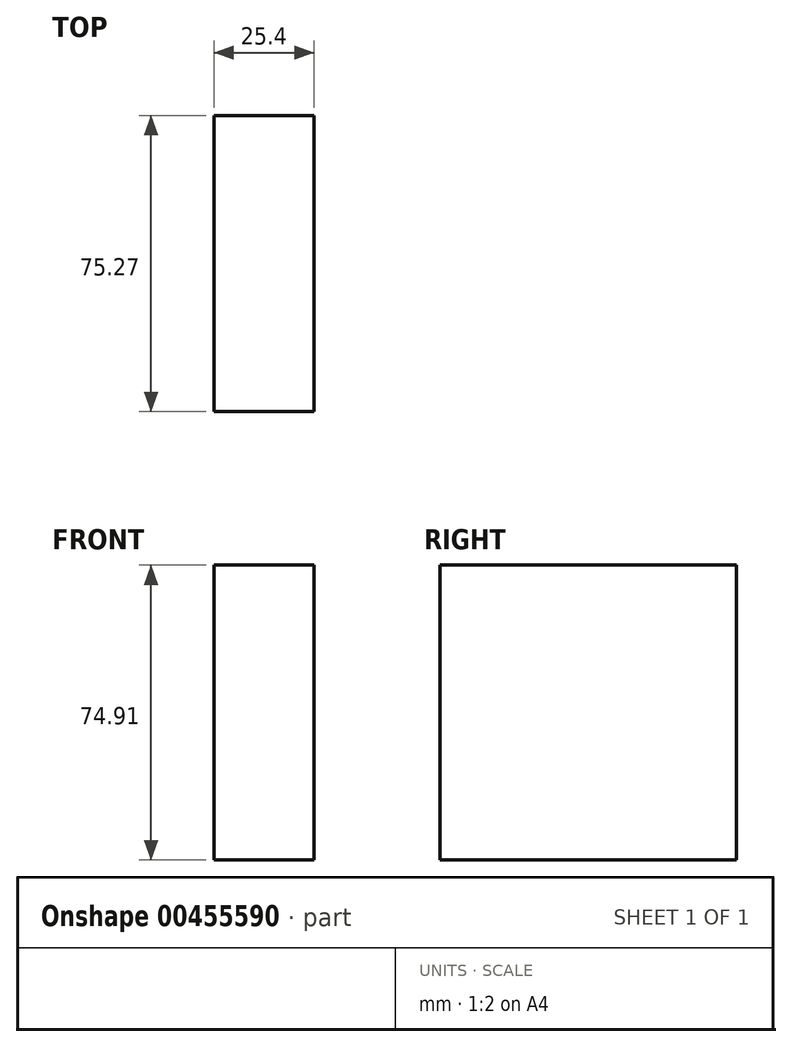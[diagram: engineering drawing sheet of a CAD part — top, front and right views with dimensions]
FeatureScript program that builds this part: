
annotation { "Feature Type Name" : "Feature", "Feature Type Description" : "" }
export const myFeature = defineFeature(function(context is Context, id is Id, definition is map)
    precondition{}
    {
        {
            var Q0;
            Q0=qCreatedBy(makeId("Right.planeOp"),FACE);
            var sketch = newSketch(context, id + "F0", { "sketchPlane" : qUnion([Q0])});
            skLineSegment(sketch, "E0.bottom", {"start": v(0, 0) * mm, "end": v(-75.27, 0) * mm});
            skLineSegment(sketch, "E0.top", {"start": v(0, 74.9) * mm, "end": v(-75.27, 74.9) * mm});
            skLineSegment(sketch, "E0.left", {"start": v(0, 0) * mm, "end": v(0, 74.9) * mm});
            skLineSegment(sketch, "E0.right", {"start": v(-75.27, 0) * mm, "end": v(-75.27, 74.9) * mm});
            skSolve(sketch);
        }
        {
            var Q0;
            Q0 = qSketchRegion(id + "F0", true);
            extrude(context, id + "F1", {"entities" : qUnion([Q0]), "oppositeDirection" : true, "depth" : 25.4 * mm});
        }
    });
